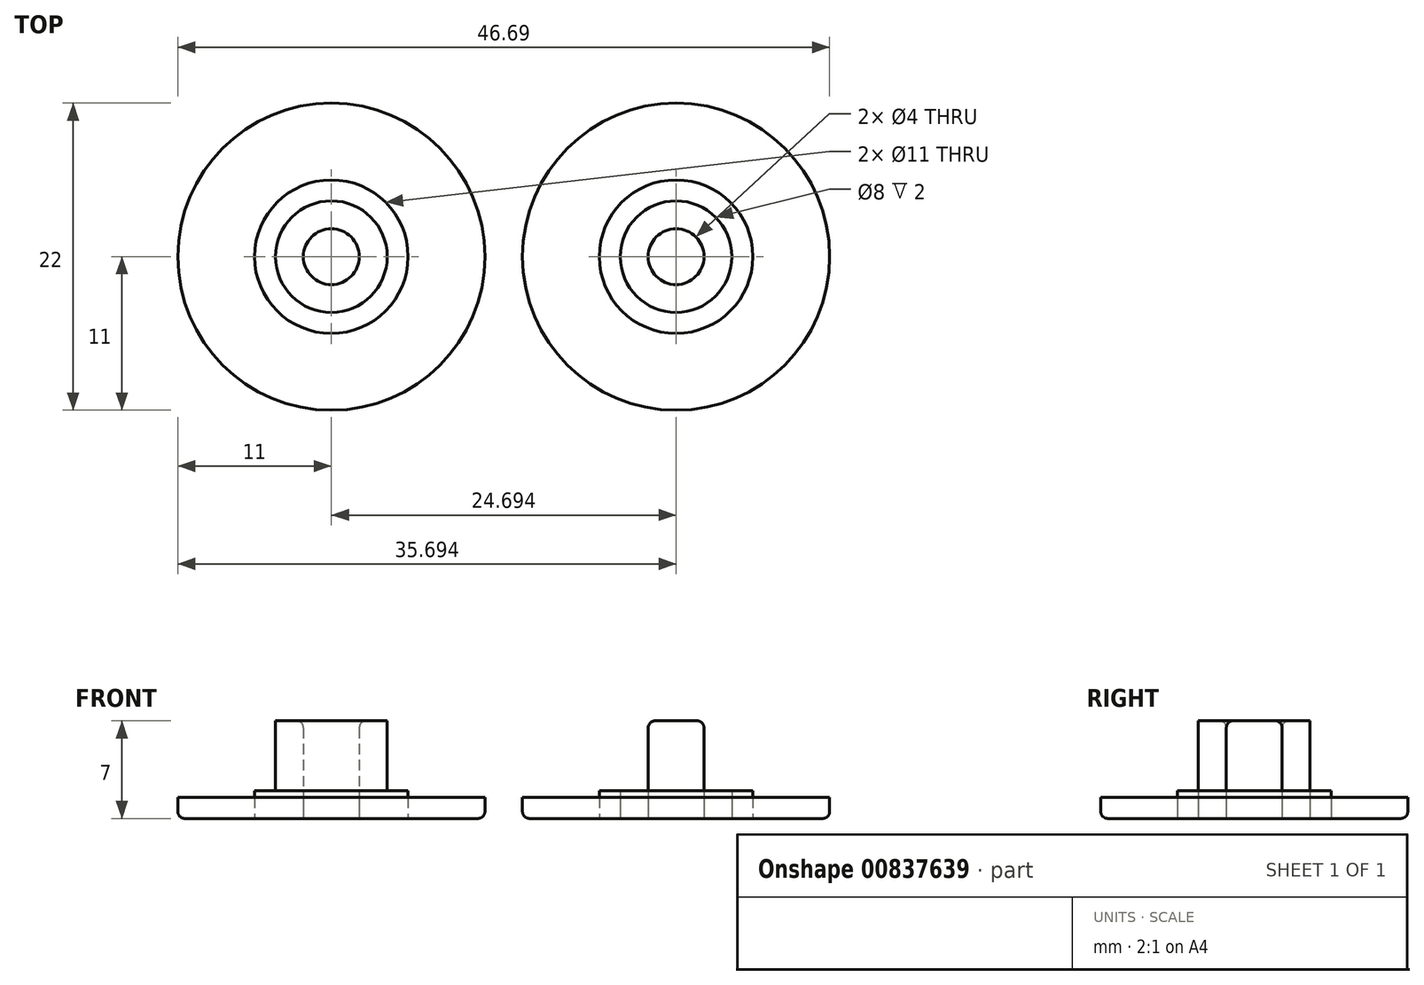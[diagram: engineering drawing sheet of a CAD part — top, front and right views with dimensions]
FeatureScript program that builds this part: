
annotation { "Feature Type Name" : "Feature", "Feature Type Description" : "" }
export const myFeature = defineFeature(function(context is Context, id is Id, definition is map)
    precondition{}
    {
        {
            var Q0;
            Q0=qCreatedBy(makeId("Top.planeOp"),FACE);
            var sketch = newSketch(context, id + "F0", { "sketchPlane" : qUnion([Q0])});
            skCircle(sketch, "E0", {"center": v(0, 0) * mm, "radius": 11 * mm});
            skCircle(sketch, "E1", {"center": v(0, 0) * mm, "radius": 5.5 * mm});
            skCircle(sketch, "E2", {"center": v(0, 0) * mm, "radius": 4 * mm});
            skCircle(sketch, "E3", {"center": v(0, 0) * mm, "radius": 2 * mm});
            skCircle(sketch, "E4", {"center": v(24.7, 0) * mm, "radius": 11 * mm});
            skCircle(sketch, "E5", {"center": v(24.7, 0) * mm, "radius": 5.5 * mm});
            skCircle(sketch, "E6", {"center": v(24.7, 0) * mm, "radius": 4 * mm});
            skCircle(sketch, "E7", {"center": v(24.7, 0) * mm, "radius": 2 * mm});
            skSolve(sketch);
        }
        {
            var Q0;
            Q0=makeQuery(id+"F0.imprint","IMPRINT",FACE,{"disambiguationData":[TD([[makeQuery(id+"F0.imprint","IMPRINT",EDGE,{"derivedFrom":sQuery(id+"F0.wireOp",EDGE,"E0")}),1.0]])]});
            var Q1;
            Q1=makeQuery(id+"F0.imprint","IMPRINT",FACE,{"disambiguationData":[TD([[makeQuery(id+"F0.imprint","IMPRINT",EDGE,{"derivedFrom":sQuery(id+"F0.wireOp",EDGE,"E4")}),1.0]])]});
            extrude(context, id + "F1", {"entities" : qUnion([Q0, Q1]), "depth" : 1.5 * mm, "offsetDistance" : 25 * mm});
        }
        {
            var Q0;
            Q0=makeQuery(id+"F0.imprint","IMPRINT",FACE,{"disambiguationData":[TD([[makeQuery(id+"F0.imprint","IMPRINT",EDGE,{"derivedFrom":sQuery(id+"F0.wireOp",EDGE,"E1")}),1.0]])]});
            var Q1;
            Q1=makeQuery(id+"F0.imprint","IMPRINT",FACE,{"disambiguationData":[TD([[makeQuery(id+"F0.imprint","IMPRINT",EDGE,{"derivedFrom":sQuery(id+"F0.wireOp",EDGE,"E5")}),1.0]])]});
            extrude(context, id + "F2", {"entities" : qUnion([Q0, Q1]), "depth" : 2 * mm, "offsetDistance" : 25 * mm});
        }
        {
            var Q0;
            Q0=makeQuery(id+"F0.imprint","IMPRINT",FACE,{"disambiguationData":[TD([[makeQuery(id+"F0.imprint","IMPRINT",EDGE,{"derivedFrom":sQuery(id+"F0.wireOp",EDGE,"E2")}),1.0]])]});
            var Q1;
            Q1=makeQuery(id+"F0.imprint","IMPRINT",FACE,{"disambiguationData":[TD([[makeQuery(id+"F0.imprint","IMPRINT",EDGE,{"derivedFrom":sQuery(id+"F0.wireOp",EDGE,"E7")}),1.0]])]});
            extrude(context, id + "F3", {"entities" : qUnion([Q0, Q1]), "operationType" : NewBodyOperationType.ADD, "depth" : 7 * mm, "offsetDistance" : 25 * mm});
        }
        {
            var Q0;
            Q0=makeQuery(id+"F0.imprint","IMPRINT",FACE,{"disambiguationData":[TD([[makeQuery(id+"F0.imprint","IMPRINT",EDGE,{"derivedFrom":sQuery(id+"F0.wireOp",EDGE,"E3")}),1.0]])]});
            var Q1;
            Q1=makeQuery(id+"F0.imprint","IMPRINT",FACE,{"disambiguationData":[TD([[makeQuery(id+"F0.imprint","IMPRINT",EDGE,{"derivedFrom":sQuery(id+"F0.wireOp",EDGE,"E6")}),1.0]])]});
            extrude(context, id + "F4", {"entities" : qUnion([Q0, Q1]), "depth" : 1.5 * mm, "offsetDistance" : 25 * mm});
        }
        {
            var Q0;
            Q0=makeQuery(id+"F3.opExtrude","CAP_EDGE",EDGE,{"disambiguationData":[OSD([sQuery(id+"F0.wireOp",EDGE,"E3")])],"isStart":false});
            var Q1;
            Q1=makeQuery(id+"F3.opExtrude","CAP_EDGE",EDGE,{"disambiguationData":[OSD([sQuery(id+"F0.wireOp",EDGE,"E7")])],"isStart":false});
            fillet(context, id + "F5", {"entities" : qUnion([Q0, Q1]), "radius" : .5 * mm, "tangentPropagation" : true, "allowEdgeOverflow" : false});
        }
        {
            var Q0;
            Q0=makeQuery(id+"F1.opExtrude","CAP_EDGE",EDGE,{"disambiguationData":[OSD([sQuery(id+"F0.wireOp",EDGE,"E4")])],"isStart":true});
            var Q1;
            Q1=makeQuery(id+"F1.opExtrude","CAP_EDGE",EDGE,{"disambiguationData":[OSD([sQuery(id+"F0.wireOp",EDGE,"E0")])],"isStart":true});
            fillet(context, id + "F6", {"entities" : qUnion([Q0, Q1]), "radius" : .5 * mm, "tangentPropagation" : true, "allowEdgeOverflow" : false});
        }
    });
